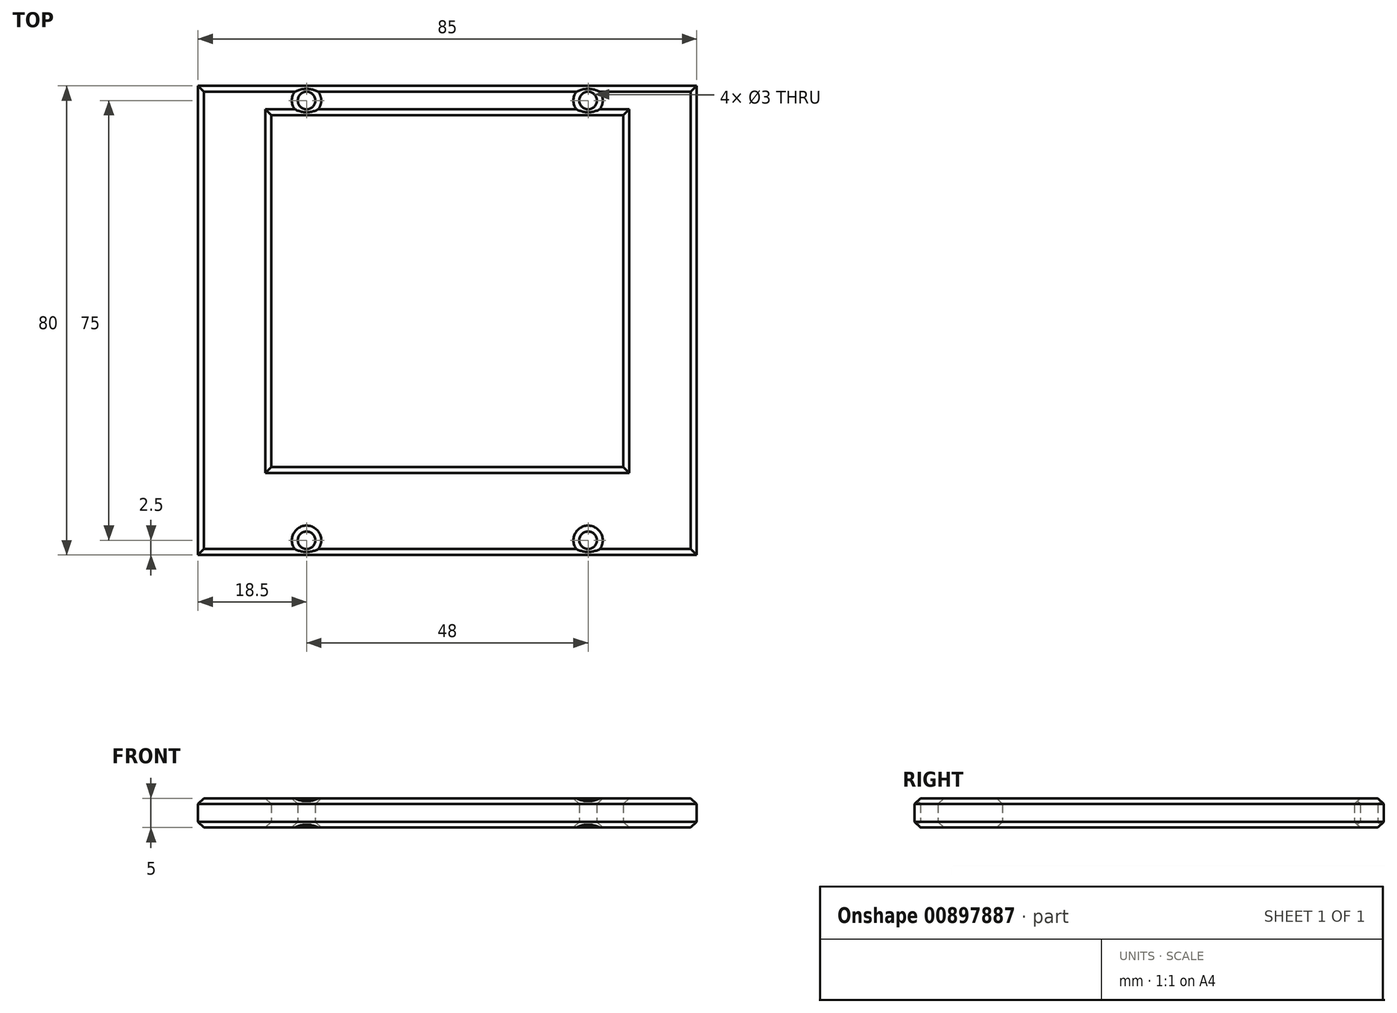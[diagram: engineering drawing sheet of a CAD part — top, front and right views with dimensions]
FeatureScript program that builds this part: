
annotation { "Feature Type Name" : "Feature", "Feature Type Description" : "" }
export const myFeature = defineFeature(function(context is Context, id is Id, definition is map)
    precondition{}
    {
        {
            var Q0;
            Q0=qCreatedBy(makeId("Top.planeOp"),FACE);
            var sketch = newSketch(context, id + "F0", { "sketchPlane" : qUnion([Q0])});
            skLineSegment(sketch, "E0.bottom", {"start": v(-42.5, 40) * mm, "end": v(42.5, 40) * mm});
            skLineSegment(sketch, "E0.top", {"start": v(-42.5, -40) * mm, "end": v(42.5, -40) * mm});
            skLineSegment(sketch, "E0.left", {"start": v(-42.5, 40) * mm, "end": v(-42.5, -40) * mm});
            skLineSegment(sketch, "E0.right", {"start": v(42.5, 40) * mm, "end": v(42.5, -40) * mm});
            skCircle(sketch, "E1", {"center": v(24, 37.5) * mm, "radius": 1.5 * mm});
            skCircle(sketch, "E2.MirrorC", {"center": v(-24, 37.5) * mm, "radius": 1.5 * mm});
            skCircle(sketch, "E3.MirrorC", {"center": v(-24, -37.5) * mm, "radius": 1.5 * mm});
            skCircle(sketch, "E4.MirrorC", {"center": v(24, -37.5) * mm, "radius": 1.5 * mm});
            skLineSegment(sketch, "E5.bottom", {"start": v(-30, 35) * mm, "end": v(30, 35) * mm});
            skLineSegment(sketch, "E5.top", {"start": v(-30, -25) * mm, "end": v(30, -25) * mm});
            skLineSegment(sketch, "E5.left", {"start": v(-30, 35) * mm, "end": v(-30, -25) * mm});
            skLineSegment(sketch, "E5.right", {"start": v(30, 35) * mm, "end": v(30, -25) * mm});
            skLineSegment(sketch, "E6", {"start": v(-24, 37.5) * mm, "end": v(24, 37.5) * mm, "construction": true});
            skLineSegment(sketch, "E7", {"start": v(24, -37.5) * mm, "end": v(-24, -37.5) * mm, "construction": true});
            skLineSegment(sketch, "E8", {"start": v(-24, -37.5) * mm, "end": v(-24, 37.5) * mm, "construction": true});
            skLineSegment(sketch, "E9", {"start": v(24, 37.5) * mm, "end": v(24, -37.5) * mm, "construction": true});
            skSolve(sketch);
        }
        {
            var Q0;
            Q0=makeQuery(id+"F0.imprint","IMPRINT",FACE,{"disambiguationData":[TD([[makeQuery(id+"F0.imprint","IMPRINT",EDGE,{"derivedFrom":sQuery(id+"F0.wireOp",EDGE,"E0.bottom")}),-1.0]])]});
            extrude(context, id + "F1", {"entities" : qUnion([Q0]), "depth" : 5 * mm, "offsetDistance" : 25 * mm});
        }
        {
            var Q0;
            Q0=makeQuery(id+"F1.opExtrude","CAP_FACE",FACE,{"disambiguationData":[OSD([sQuery(id+"F0.wireOp",EDGE,"E0.bottom"),sQuery(id+"F0.wireOp",EDGE,"E0.top"),sQuery(id+"F0.wireOp",EDGE,"E0.left"),sQuery(id+"F0.wireOp",EDGE,"E0.right"),sQuery(id+"F0.wireOp",EDGE,"E2.MirrorC"),sQuery(id+"F0.wireOp",EDGE,"E1"),sQuery(id+"F0.wireOp",EDGE,"E3.MirrorC"),sQuery(id+"F0.wireOp",EDGE,"E4.MirrorC"),sQuery(id+"F0.wireOp",EDGE,"E5.bottom"),sQuery(id+"F0.wireOp",EDGE,"E5.top"),sQuery(id+"F0.wireOp",EDGE,"E5.left"),sQuery(id+"F0.wireOp",EDGE,"E5.right")])],"isStart":false});
            var Q1;
            Q1=makeQuery(id+"F1.opExtrude","CAP_FACE",FACE,{"disambiguationData":[OSD([sQuery(id+"F0.wireOp",EDGE,"E0.bottom"),sQuery(id+"F0.wireOp",EDGE,"E0.top"),sQuery(id+"F0.wireOp",EDGE,"E0.left"),sQuery(id+"F0.wireOp",EDGE,"E0.right"),sQuery(id+"F0.wireOp",EDGE,"E2.MirrorC"),sQuery(id+"F0.wireOp",EDGE,"E1"),sQuery(id+"F0.wireOp",EDGE,"E3.MirrorC"),sQuery(id+"F0.wireOp",EDGE,"E4.MirrorC"),sQuery(id+"F0.wireOp",EDGE,"E5.bottom"),sQuery(id+"F0.wireOp",EDGE,"E5.top"),sQuery(id+"F0.wireOp",EDGE,"E5.left"),sQuery(id+"F0.wireOp",EDGE,"E5.right")])],"isStart":true});
            chamfer(context, id + "F2", {"entities" : qUnion([Q0, Q1]), "width" : 1 * mm, "tangentPropagation" : true});
        }
    });
